# Revit family: Drain_Floor_Adjustable_Zurn-FD2210
name_source: partatom
category: Plumbing Fixtures
units: mm (PartAtom-declared; Revit-internal decimal feet)

## family parameters
Always vertical = Yes
Cut with Voids When Loaded = No
Maintain Annotation Orientation = No
OmniClass Number = 23.70.50.21.24.14
OmniClass Title = Deck Waste Water Drains
Part Type = Normal
Room Calculation Point = No
Round Connector Dimension = Use Radius
Shared = No
Work Plane-Based = No

## types (6) — shared parameters
Assembly Code = D2030300
CW Connection = No
Default Elevation = 25 "
Description = Adjustable Floor Drain
Grate = 1.72 "
Grate Open Area Sq.in = 7 "
HW Connection = No
Head and Grate = Bronze - Zurn - Polished Nickel
Manufacturer = Zurn Water, LLC
Manufacurer Brand = Zurn
Model = FD2210
Modified Date = 10/24/2025
Product Documentation Link = https://files.zurn.com
Product Page URL = https://www.zurn.com
Product data url = https://www.bimobject.com
URL = www.zurn.com
Vent Connection = No
WFU = 1
Waste Connection = Yes
Width = 5.188 "
zero-valued in all types: CWFU, HWFU

## per-type parameters (varying)
| type | Body Height (B) | Main Material | Pipe Size A  (Nominal Radius) | Pipe Size A (Inner Radius) | Pipe Size A (Outer Radius) |
| FD2210-PV2-2 Inch Outlet | 2.125 " | Polyvinyl Chloride - Zurn - Polished | 1 " | 1.034 " | 1.188 " |
| FD2210-PV3-3 Inch Outlet | 2.188 " | Polyvinyl Chloride - Zurn - Polished | 1.5 " | 1.534 " | 1.75 " |
| FD2210-PV4-4 Inch Outlet | 2.188 " | Polyvinyl Chloride - Zurn - Polished | 2 " | 2.013 " | 2.25 " |
| FD2210-AB2-2 Inch Outlet | 2.125 " | Acrylonitrile Butadiene Styrene - Zurn - Polished | 1 " | 1.034 " | 1.188 " |
| FD2210-AB3-3 Inch Outlet | 2.188 " | Acrylonitrile Butadiene Styrene - Zurn - Polished | 1.5 " | 1.534 " | 1.75 " |
| FD2210-AB4-4 Inch Outlet | 2.188 " | Acrylonitrile Butadiene Styrene - Zurn - Polished | 2 " | 2.013 " | 2.25 " |

## geometry (parser evidence)
native form markers: Sweep x4
no freeform markers — native parametric forms only
